# Revit family: Hager-VECTOR-Surface_mounted-IP65-With_Cover-With_DIN-NoHosted-AT-de
name_source: partatom
category: Electrical Equipment
units: mm (PartAtom-declared; Revit-internal decimal feet)

## family parameters
Always vertical = Yes
Cut with Voids When Loaded = No
Maintain Annotation Orientation = No
Panel Configuration = Two Columns, Circuits Across
Part Type = Panelboard
Room Calculation Point = No
Round Connector Dimension = Use Diameter
Shared = No
Work Plane-Based = Yes

## types (30) — shared parameters
Code hager = ADD-EC000214_EU
Default Elevation = 1200 mm
EF000003 - Montageart = Aufputz
EF000007 - Farbe = grau
EF000024 - UV-beständig = No
EF000116 - RAL-Nummer = 7035
EF000118 - Mit Montageplatte = No
EF001062 - EMV-Ausführung = No
EF001088 - Anbaumöglichkeit = Yes
EF001134 - DIN-Schiene = Yes
EF004462 - Art der Schließung = sonstige
EF005474 - Schutzart (IP) = IP65
EF006244 - Transparenter Deckel/Tür = Yes
EF006306 - Mit Schloss = No
EF015941 - Signaldurchlassende Tür = Yes
ETIM class code = EC000214
ETIM class name = Small distribution board
HG000001-Anzahl der Spalten = 1
HG000002-Mit tür = Yes
HG000003-Bereich = VECTOR
HG000005-Dicke = 2 mm  [stored 0.00656168 ft]
HG000006-Unterputz = No
HG000009-Doppelflügeligen Tür = No
HG000010-Asymmetrische Türen = No
HG000011-Leere Reihen von unten = No
HG000012-Türschwenkwinkel = 90.00°
HG000013-Tür links = No
HG000014-Tür rechts = Yes
HG000015-Sichtbarkeit der Türöffnung = Yes
HG000016-3D-Türsichtbarkeit = Yes
HG000017-Distanz zwischen den Polen = 18 mm  [stored 0.0590551 ft]
HG000060-RAL-number = 7035
HG000099-Onfly Template ID-de-AT = 507532
Manufacturer = Hager
Name BIM&CO = Electricity
Name hager = ADD_Enclosures_EC000214
Reference = Template-Enclosure_EU-EC000214
Uniformat = Low Tension Service & Dist.
Uniformat code = D501001
zero-valued in all types: EF000218 - Einbautiefe, EF000332 - Einbauhöhe, EF000846 - Einbaubreite, EF001131 - Innentiefe, HG000007-Anzahl der leeren Spalten, HG000008-Anzahl der leeren Reihen

## per-type parameters (varying)
| type | BC_METADATA | EF000008 - Breite | EF000040 - Höhe | EF000049 - Tiefe | EF000266 - Anzahl der Reihen | EF002950 - Breite in Teilungseinheiten | EF009212 - Ausführung Deckel | EF015776 - Erdungsklemmenblock | EF015777 - Neutralleiterklemmenblock | HG000004-Herstellerreferenz | HGEF000266-Anzahl der Reihen | HGEF0002950-Breite in Teilungseinheiten |
| VECTOR-Surface_mounted_W310_H302_D151_12_Modular_Spacing-VE112SN | {"ObjectGuid":"2ca3431b-ede5-43e4-b361-639836267a08","ModelGuid":"e9147650-b0db-4066-9894-f949c9315221","VariantGuid":"8888d621-9c8e-4da0-988e-402acc34b242","Revision":"#6","VariantName":"VECTOR-Surface_mounted_W310_H302_D151_12_Modular_Spacing-VE112SN"} | 310 mm  [stored 1.01706 ft] | 302 mm  [stored 0.990814 ft] | 151 mm  [stored 0.495407 ft] | 1 | 12 | geschlossen | No | No | VE112SN | 1 | 12 |
| VECTOR-Surface_mounted_W418_H302_D151_18_Modular_Spacing-VE118DN | {"ObjectGuid":"2ca3431b-ede5-43e4-b361-639836267a08","ModelGuid":"e9147650-b0db-4066-9894-f949c9315221","VariantGuid":"2255085c-7b54-457e-b0bd-47974c23ed64","Revision":"#6","VariantName":"VECTOR-Surface_mounted_W418_H302_D151_18_Modular_Spacing-VE118DN"} | 418 mm  [stored 1.37139 ft] | 302 mm  [stored 0.990814 ft] | 151 mm  [stored 0.495407 ft] | 1 | 18 | geschlossen | Yes | Yes | VE118DN | 1 | 18 |
| VECTOR-Surface_mounted_W418_H302_D151_18_Modular_Spacing-VE118PN | {"ObjectGuid":"2ca3431b-ede5-43e4-b361-639836267a08","ModelGuid":"e9147650-b0db-4066-9894-f949c9315221","VariantGuid":"f08cfaf6-9260-49d8-b64c-6e9bba3e7dfa","Revision":"#6","VariantName":"VECTOR-Surface_mounted_W418_H302_D151_18_Modular_Spacing-VE118PN"} | 418 mm  [stored 1.37139 ft] | 302 mm  [stored 0.990814 ft] | 151 mm  [stored 0.495407 ft] | 1 | 18 | geschlossen | No | No | VE118PN | 1 | 18 |
| VECTOR-Surface_mounted_W418_H302_D151_18_Modular_Spacing-VE118SN | {"ObjectGuid":"2ca3431b-ede5-43e4-b361-639836267a08","ModelGuid":"e9147650-b0db-4066-9894-f949c9315221","VariantGuid":"ac63022f-723b-44fb-bf8d-22d4fddc574f","Revision":"#6","VariantName":"VECTOR-Surface_mounted_W418_H302_D151_18_Modular_Spacing-VE118SN"} | 418 mm  [stored 1.37139 ft] | 302 mm  [stored 0.990814 ft] | 151 mm  [stored 0.495407 ft] | 1 | 18 | geschlossen | No | No | VE118SN | 1 | 18 |
| VECTOR-Surface_mounted_W310_H427_D151_12_Modular_Spacing-VE212DN | {"ObjectGuid":"2ca3431b-ede5-43e4-b361-639836267a08","ModelGuid":"e9147650-b0db-4066-9894-f949c9315221","VariantGuid":"0459b0d6-8653-4dfc-93c1-d25f7f7cb77a","Revision":"#6","VariantName":"VECTOR-Surface_mounted_W310_H427_D151_12_Modular_Spacing-VE212DN"} | 310 mm  [stored 1.01706 ft] | 427 mm  [stored 1.40092 ft] | 151 mm  [stored 0.495407 ft] | 2 | 12 | geschlossen | Yes | Yes | VE212DN | 2 | 12 |
| VECTOR-Surface_mounted_W310_H427_D151_12_Modular_Spacing-VE212PN | {"ObjectGuid":"2ca3431b-ede5-43e4-b361-639836267a08","ModelGuid":"e9147650-b0db-4066-9894-f949c9315221","VariantGuid":"523afe67-4028-4d0e-818f-3013cf45b492","Revision":"#6","VariantName":"VECTOR-Surface_mounted_W310_H427_D151_12_Modular_Spacing-VE212PN"} | 310 mm  [stored 1.01706 ft] | 427 mm  [stored 1.40092 ft] | 151 mm  [stored 0.495407 ft] | 2 | 12 | geschlossen | No | No | VE212PN | 2 | 12 |
| VECTOR-Surface_mounted_W310_H427_D151_12_Modular_Spacing-VE212SN | {"ObjectGuid":"2ca3431b-ede5-43e4-b361-639836267a08","ModelGuid":"e9147650-b0db-4066-9894-f949c9315221","VariantGuid":"d4d88b68-1471-45c4-a376-102aa1e81820","Revision":"#6","VariantName":"VECTOR-Surface_mounted_W310_H427_D151_12_Modular_Spacing-VE212SN"} | 310 mm  [stored 1.01706 ft] | 427 mm  [stored 1.40092 ft] | 151 mm  [stored 0.495407 ft] | 2 | 12 | geschlossen | No | No | VE212SN | 2 | 12 |
| VECTOR-Surface_mounted_W418_H452_D151_18_Modular_Spacing-VE218DN | {"ObjectGuid":"2ca3431b-ede5-43e4-b361-639836267a08","ModelGuid":"e9147650-b0db-4066-9894-f949c9315221","VariantGuid":"e5a2d0ad-cfda-4ab9-9a08-67fa7a55af02","Revision":"#6","VariantName":"VECTOR-Surface_mounted_W418_H452_D151_18_Modular_Spacing-VE218DN"} | 418 mm  [stored 1.37139 ft] | 452 mm  [stored 1.48294 ft] | 151 mm  [stored 0.495407 ft] | 2 | 18 | geschlossen | Yes | Yes | VE218DN | 2 | 18 |
| VECTOR-Surface_mounted_W418_H452_D151_18_Modular_Spacing-VE218PN | {"ObjectGuid":"2ca3431b-ede5-43e4-b361-639836267a08","ModelGuid":"e9147650-b0db-4066-9894-f949c9315221","VariantGuid":"461fdd18-038b-4fc2-9f9c-c080a8d97ce4","Revision":"#6","VariantName":"VECTOR-Surface_mounted_W418_H452_D151_18_Modular_Spacing-VE218PN"} | 418 mm  [stored 1.37139 ft] | 452 mm  [stored 1.48294 ft] | 151 mm  [stored 0.495407 ft] | 2 | 18 | geschlossen | No | No | VE218PN | 2 | 18 |
| VECTOR-Surface_mounted_W110_H175_D93_3_Modular_Spacing-VE103D | {"ObjectGuid":"2ca3431b-ede5-43e4-b361-639836267a08","ModelGuid":"e9147650-b0db-4066-9894-f949c9315221","VariantGuid":"4e4401fb-63c9-47ed-beb4-b90d650783e4","Revision":"#6","VariantName":"VECTOR-Surface_mounted_W110_H175_D93_3_Modular_Spacing-VE103D"} | 110 mm  [stored 0.360892 ft] | 175 mm  [stored 0.574147 ft] | 93 mm  [stored 0.305118 ft] | 1 | 3 | geschlossen | Yes | No | VE103D | 1 | 3 |
| VECTOR-Surface_mounted_W111_H175_D93_3_Modular_Spacing-VE103SN | {"ObjectGuid":"2ca3431b-ede5-43e4-b361-639836267a08","ModelGuid":"e9147650-b0db-4066-9894-f949c9315221","VariantGuid":"2fecb53a-e2f3-4ccc-8213-17dc970e4886","Revision":"#6","VariantName":"VECTOR-Surface_mounted_W111_H175_D93_3_Modular_Spacing-VE103SN"} | 111 mm | 175 mm  [stored 0.574147 ft] | 93 mm  [stored 0.305118 ft] | 1 | 3 | mit Ausschnitt | No | No | VE103SN | 1 | 3 |
| VECTOR-Surface_mounted_W164_H190_D113_6_Modular_Spacing-VE106D | {"ObjectGuid":"2ca3431b-ede5-43e4-b361-639836267a08","ModelGuid":"e9147650-b0db-4066-9894-f949c9315221","VariantGuid":"e74a29a5-225c-4eb1-965c-0f1d2069f5e3","Revision":"#6","VariantName":"VECTOR-Surface_mounted_W164_H190_D113_6_Modular_Spacing-VE106D"} | 164 mm  [stored 0.538058 ft] | 190 mm  [stored 0.62336 ft] | 113 mm  [stored 0.370735 ft] | 1 | 6 | geschlossen | Yes | No | VE106D | 1 | 6 |
| VECTOR-Surface_mounted_W165_H190_D113_6_Modular_Spacing-VE106PN | {"ObjectGuid":"2ca3431b-ede5-43e4-b361-639836267a08","ModelGuid":"e9147650-b0db-4066-9894-f949c9315221","VariantGuid":"0bb8eb3b-9e5a-41c6-a0de-03b3143ba9d9","Revision":"#6","VariantName":"VECTOR-Surface_mounted_W165_H190_D113_6_Modular_Spacing-VE106PN"} | 165 mm | 190 mm  [stored 0.62336 ft] | 113 mm  [stored 0.370735 ft] | 1 | 6 | geschlossen | No | No | VE106PN | 1 | 6 |
| VECTOR-Surface_mounted_W111_H175_D93_3_Modular_Spacing-VE103PN | {"ObjectGuid":"2ca3431b-ede5-43e4-b361-639836267a08","ModelGuid":"e9147650-b0db-4066-9894-f949c9315221","VariantGuid":"ebe3d29a-e327-4462-889c-eecff40864ea","Revision":"#6","VariantName":"VECTOR-Surface_mounted_W111_H175_D93_3_Modular_Spacing-VE103PN"} | 111 mm | 175 mm  [stored 0.574147 ft] | 93 mm  [stored 0.305118 ft] | 1 | 3 | mit Ausschnitt | No | No | VE103PN | 1 | 3 |
| VECTOR-Surface_mounted_W165_H190_D113_6_Modular_Spacing-VE106SN | {"ObjectGuid":"2ca3431b-ede5-43e4-b361-639836267a08","ModelGuid":"e9147650-b0db-4066-9894-f949c9315221","VariantGuid":"964ae978-ef3e-44d5-9041-0c7ab3826e18","Revision":"#6","VariantName":"VECTOR-Surface_mounted_W165_H190_D113_6_Modular_Spacing-VE106SN"} | 165 mm | 190 mm  [stored 0.62336 ft] | 113 mm  [stored 0.370735 ft] | 1 | 6 | mit Ausschnitt | No | No | VE106SN | 1 | 6 |
| VECTOR-Surface_mounted_W236_H210_D114_10_Modular_Spacing-VE110D | {"ObjectGuid":"2ca3431b-ede5-43e4-b361-639836267a08","ModelGuid":"e9147650-b0db-4066-9894-f949c9315221","VariantGuid":"c44f89cd-81e1-48c4-b718-e17494ff81c2","Revision":"#6","VariantName":"VECTOR-Surface_mounted_W236_H210_D114_10_Modular_Spacing-VE110D"} | 236 mm | 210 mm  [stored 0.688976 ft] | 114 mm  [stored 0.374016 ft] | 1 | 10 | geschlossen | Yes | No | VE110D | 1 | 10 |
| VECTOR-Surface_mounted_W237_H210_D114_10_Modular_Spacing-VE110PN | {"ObjectGuid":"2ca3431b-ede5-43e4-b361-639836267a08","ModelGuid":"e9147650-b0db-4066-9894-f949c9315221","VariantGuid":"f24d1746-938a-4117-8d5a-ef2bdee456fc","Revision":"#6","VariantName":"VECTOR-Surface_mounted_W237_H210_D114_10_Modular_Spacing-VE110PN"} | 237 mm  [stored 0.777559 ft] | 210 mm  [stored 0.688976 ft] | 114 mm  [stored 0.374016 ft] | 1 | 10 | geschlossen | No | No | VE110PN | 1 | 10 |
| VECTOR-Surface_mounted_W237_H210_D114_10_Modular_Spacing-VE110SN | {"ObjectGuid":"2ca3431b-ede5-43e4-b361-639836267a08","ModelGuid":"e9147650-b0db-4066-9894-f949c9315221","VariantGuid":"421b81b2-9959-4b52-9fe3-20f2d3a9e14d","Revision":"#6","VariantName":"VECTOR-Surface_mounted_W237_H210_D114_10_Modular_Spacing-VE110SN"} | 237 mm  [stored 0.777559 ft] | 210 mm  [stored 0.688976 ft] | 114 mm  [stored 0.374016 ft] | 1 | 10 | geschlossen | No | No | VE110SN | 1 | 10 |
| VECTOR-Surface_mounted_W310_H302_D151_12_Modular_Spacing-VE112DN | {"ObjectGuid":"2ca3431b-ede5-43e4-b361-639836267a08","ModelGuid":"e9147650-b0db-4066-9894-f949c9315221","VariantGuid":"95034a70-024a-41f7-90e0-3cedf5c75324","Revision":"#6","VariantName":"VECTOR-Surface_mounted_W310_H302_D151_12_Modular_Spacing-VE112DN"} | 310 mm  [stored 1.01706 ft] | 302 mm  [stored 0.990814 ft] | 151 mm  [stored 0.495407 ft] | 1 | 12 | geschlossen | Yes | Yes | VE112DN | 1 | 12 |
| VECTOR-Surface_mounted_W310_H302_D151_12_Modular_Spacing-VE112PN | {"ObjectGuid":"2ca3431b-ede5-43e4-b361-639836267a08","ModelGuid":"e9147650-b0db-4066-9894-f949c9315221","VariantGuid":"45cb9261-e062-4380-bdab-0ea4899d0d10","Revision":"#6","VariantName":"VECTOR-Surface_mounted_W310_H302_D151_12_Modular_Spacing-VE112PN"} | 310 mm  [stored 1.01706 ft] | 302 mm  [stored 0.990814 ft] | 151 mm  [stored 0.495407 ft] | 1 | 12 | geschlossen | No | No | VE112PN | 1 | 12 |
| VECTOR-Surface_mounted_W418_H452_D151_18_Modular_Spacing-VE218SN | {"ObjectGuid":"2ca3431b-ede5-43e4-b361-639836267a08","ModelGuid":"e9147650-b0db-4066-9894-f949c9315221","VariantGuid":"8c0443b4-a9a7-4b80-8320-5f6c9c17b03a","Revision":"#6","VariantName":"VECTOR-Surface_mounted_W418_H452_D151_18_Modular_Spacing-VE218SN"} | 418 mm  [stored 1.37139 ft] | 452 mm  [stored 1.48294 ft] | 151 mm  [stored 0.495407 ft] | 2 | 18 | mit Ausschnitt | No | No | VE218SN | 2 | 18 |
| VECTOR-Surface_mounted_W310_H552_D151_12_Modular_Spacing-VE312DN | {"ObjectGuid":"2ca3431b-ede5-43e4-b361-639836267a08","ModelGuid":"e9147650-b0db-4066-9894-f949c9315221","VariantGuid":"a3ff0cd5-0335-4985-b6ae-f9569b623e69","Revision":"#6","VariantName":"VECTOR-Surface_mounted_W310_H552_D151_12_Modular_Spacing-VE312DN"} | 310 mm  [stored 1.01706 ft] | 552 mm  [stored 1.81102 ft] | 151 mm  [stored 0.495407 ft] | 3 | 12 | geschlossen | Yes | Yes | VE312DN | 3 | 12 |
| VECTOR-Surface_mounted_W310_H552_D151_12_Modular_Spacing-VE312PN | {"ObjectGuid":"2ca3431b-ede5-43e4-b361-639836267a08","ModelGuid":"e9147650-b0db-4066-9894-f949c9315221","VariantGuid":"6760ba4b-73f0-4e40-b1cd-5908ed5fbdf0","Revision":"#6","VariantName":"VECTOR-Surface_mounted_W310_H552_D151_12_Modular_Spacing-VE312PN"} | 310 mm  [stored 1.01706 ft] | 552 mm  [stored 1.81102 ft] | 151 mm  [stored 0.495407 ft] | 3 | 12 | geschlossen | No | No | VE312PN | 3 | 12 |
| VECTOR-Surface_mounted_W310_H552_D151_12_Modular_Spacing-VE312SN | {"ObjectGuid":"2ca3431b-ede5-43e4-b361-639836267a08","ModelGuid":"e9147650-b0db-4066-9894-f949c9315221","VariantGuid":"a7b31476-0595-41f7-821f-468066658489","Revision":"#6","VariantName":"VECTOR-Surface_mounted_W310_H552_D151_12_Modular_Spacing-VE312SN"} | 310 mm  [stored 1.01706 ft] | 552 mm  [stored 1.81102 ft] | 151 mm  [stored 0.495407 ft] | 3 | 12 | mit Ausschnitt | No | No | VE312SN | 3 | 12 |
| VECTOR-Surface_mounted_W418_H602_D151_18_Modular_Spacing-VE318DN | {"ObjectGuid":"2ca3431b-ede5-43e4-b361-639836267a08","ModelGuid":"e9147650-b0db-4066-9894-f949c9315221","VariantGuid":"002e01d9-ca94-45ab-96b1-ed45866b7b83","Revision":"#6","VariantName":"VECTOR-Surface_mounted_W418_H602_D151_18_Modular_Spacing-VE318DN"} | 418 mm  [stored 1.37139 ft] | 602 mm  [stored 1.97507 ft] | 151 mm  [stored 0.495407 ft] | 3 | 18 | geschlossen | Yes | Yes | VE318DN | 3 | 18 |
| VECTOR-Surface_mounted_W418_H602_D151_18_Modular_Spacing-VE318PN | {"ObjectGuid":"2ca3431b-ede5-43e4-b361-639836267a08","ModelGuid":"e9147650-b0db-4066-9894-f949c9315221","VariantGuid":"ee9215e6-0b86-498e-bf0a-5c5ec1374044","Revision":"#6","VariantName":"VECTOR-Surface_mounted_W418_H602_D151_18_Modular_Spacing-VE318PN"} | 418 mm  [stored 1.37139 ft] | 602 mm  [stored 1.97507 ft] | 151 mm  [stored 0.495407 ft] | 3 | 18 | geschlossen | No | No | VE318PN | 3 | 18 |
| VECTOR-Surface_mounted_W418_H602_D151_18_Modular_Spacing-VE318SN | {"ObjectGuid":"2ca3431b-ede5-43e4-b361-639836267a08","ModelGuid":"e9147650-b0db-4066-9894-f949c9315221","VariantGuid":"ef81377f-02ba-4eb8-993f-7358a6f1ebe5","Revision":"#6","VariantName":"VECTOR-Surface_mounted_W418_H602_D151_18_Modular_Spacing-VE318SN"} | 418 mm  [stored 1.37139 ft] | 602 mm  [stored 1.97507 ft] | 151 mm  [stored 0.495407 ft] | 3 | 18 | mit Ausschnitt | No | No | VE318SN | 3 | 18 |
| VECTOR-Surface_mounted_W310_H677_D151_12_Modular_Spacing-VE412DN | {"ObjectGuid":"2ca3431b-ede5-43e4-b361-639836267a08","ModelGuid":"e9147650-b0db-4066-9894-f949c9315221","VariantGuid":"ad298743-c7b6-4329-bdf8-950e1ebe9764","Revision":"#6","VariantName":"VECTOR-Surface_mounted_W310_H677_D151_12_Modular_Spacing-VE412DN"} | 310 mm  [stored 1.01706 ft] | 677 mm  [stored 2.22113 ft] | 151 mm  [stored 0.495407 ft] | 4 | 12 | geschlossen | Yes | Yes | VE412DN | 4 | 12 |
| VECTOR-Surface_mounted_W310_H677_D151_12_Modular_Spacing-VE412PN | {"ObjectGuid":"2ca3431b-ede5-43e4-b361-639836267a08","ModelGuid":"e9147650-b0db-4066-9894-f949c9315221","VariantGuid":"946c017e-b240-4364-8449-28772d612304","Revision":"#6","VariantName":"VECTOR-Surface_mounted_W310_H677_D151_12_Modular_Spacing-VE412PN"} | 310 mm  [stored 1.01706 ft] | 677 mm  [stored 2.22113 ft] | 151 mm  [stored 0.495407 ft] | 4 | 12 | geschlossen | No | No | VE412PN | 4 | 12 |
| VECTOR-Surface_mounted_W310_H677_D151_12_Modular_Spacing-VE412SN | {"ObjectGuid":"2ca3431b-ede5-43e4-b361-639836267a08","ModelGuid":"e9147650-b0db-4066-9894-f949c9315221","VariantGuid":"59e144d2-021d-4be4-9ef9-891380ec69f0","Revision":"#6","VariantName":"VECTOR-Surface_mounted_W310_H677_D151_12_Modular_Spacing-VE412SN"} | 310 mm  [stored 1.01706 ft] | 677 mm  [stored 2.22113 ft] | 151 mm  [stored 0.495407 ft] | 4 | 12 | mit Ausschnitt | No | No | VE412SN | 4 | 12 |

note: [stored X ft] marks values corroborated as IEEE doubles in the binary element streams (Revit-internal decimal feet)

## geometry (parser evidence)
native form markers: Sweep x14
no freeform markers — native parametric forms only
